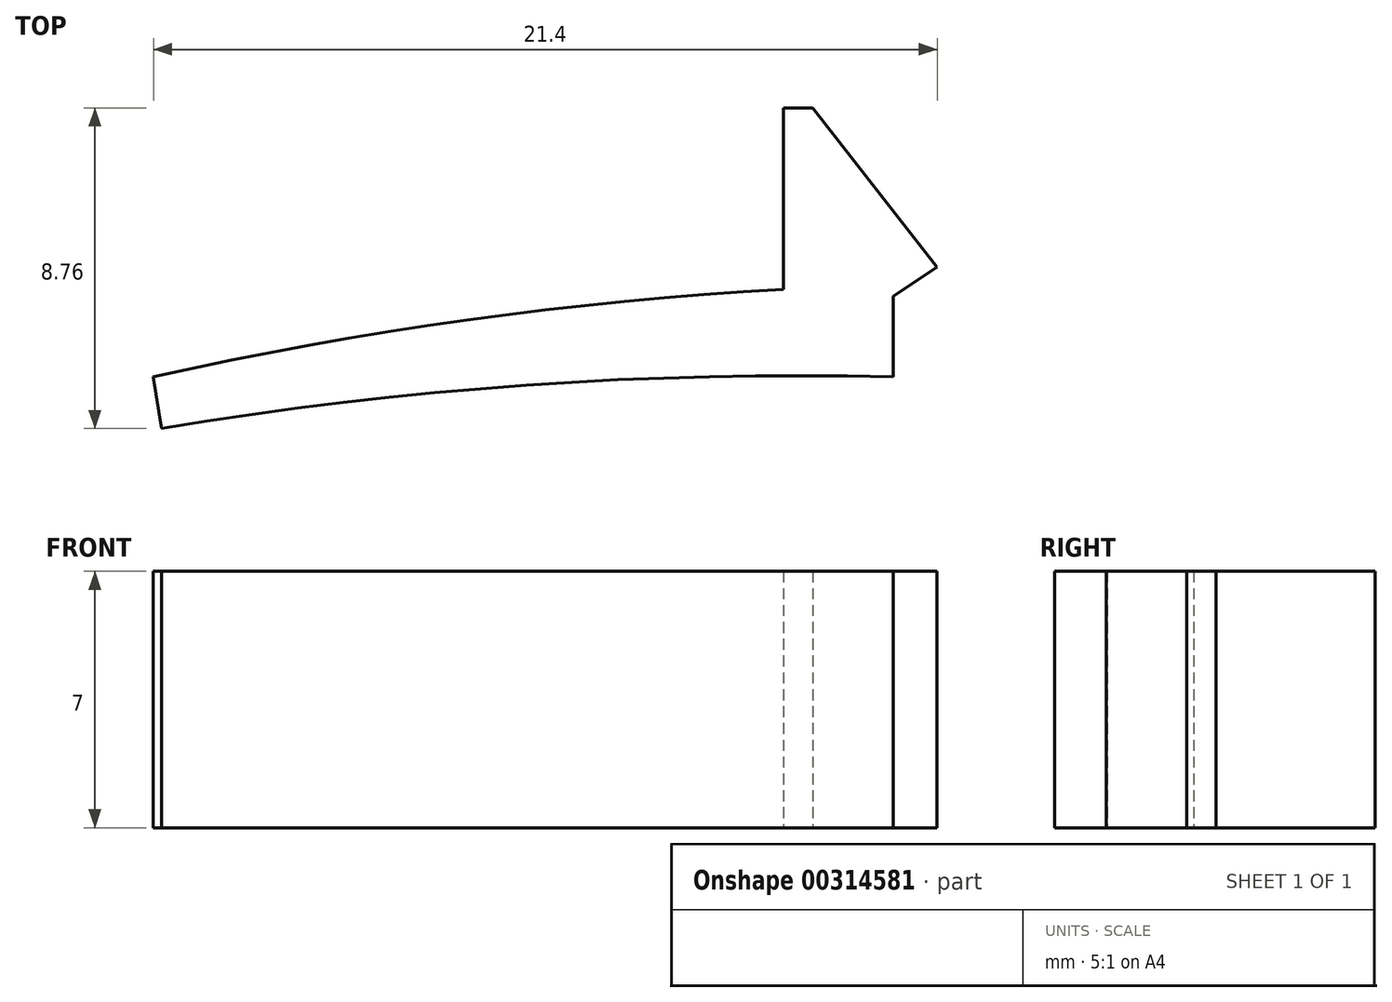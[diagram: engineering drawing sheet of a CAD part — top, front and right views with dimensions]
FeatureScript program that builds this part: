
annotation { "Feature Type Name" : "Feature", "Feature Type Description" : "" }
export const myFeature = defineFeature(function(context is Context, id is Id, definition is map)
    precondition{}
    {
        {
            var Q0;
            Q0=qCreatedBy(makeId("Top.planeOp"),FACE);
            var sketch = newSketch(context, id + "F0", { "sketchPlane" : qUnion([Q0])});
            skLineSegment(sketch, "E0.left", {"start": v(-3.95, 0) * mm, "end": v(-3.95, 0.03) * mm});
            skLineSegment(sketch, "E0.right", {"start": v(-0.95, 0) * mm, "end": v(-0.95, 2.2) * mm});
            skLineSegment(sketch, "E1", {"start": v(-0.95, 2.2) * mm, "end": v(0.25, 3) * mm});
            skLineSegment(sketch, "E2", {"start": v(0.25, 3) * mm, "end": v(-3.15, 7.35) * mm});
            skLineSegment(sketch, "E3", {"start": v(-3.15, 7.35) * mm, "end": v(-3.95, 7.35) * mm});
            skLineSegment(sketch, "E4", {"start": v(-3.95, 2.5) * mm, "end": v(-3.95, 7.35) * mm});
            skPoint(sketch, "E5.end.orphan", {"position": v(-20.95, -0.79) * mm});
            skArc(sketch, "E6", {"start": v(-0.95, 0) * mm, "mid": v(-10.97, -0.23) * mm, "end": v(-20.93, -1.4) * mm});
            skPoint(sketch, "E6.second.point", {"position": v(0, -209.8) * mm});
            skPoint(sketch, "E6.third.point", {"position": v(-20.93, -1.4) * mm});
            skPoint(sketch, "E7.end.orphan", {"position": v(-20.93, -1.73) * mm});
            skArc(sketch, "E8", {"start": v(-3.95, 2.39) * mm, "mid": v(-12.6, 1.55) * mm, "end": v(-21.15, 0) * mm});
            skLineSegment(sketch, "E9", {"start": v(-20.93, -1.4) * mm, "end": v(-21.15, 0) * mm});
            skLineSegment(sketch, "E10.trimOffspring", {"start": v(-3.95, 2.39) * mm, "end": v(-3.95, 2.5) * mm});
            skSolve(sketch);
        }
        {
            var Q0;
            {var subQ0=sQuery(id+"F0.wireOp",EDGE,"E0.right");Q0=makeQuery(id+"F0.imprint","IMPRINT",FACE,{"disambiguationData":[TD([[makeQuery(id+"F0.imprint","IMPRINT",EDGE,{"derivedFrom":subQ0}),1.0]])]});}
            extrude(context, id + "F1", {"entities" : qUnion([Q0]), "depth" : 7 * mm});
        }
    });
